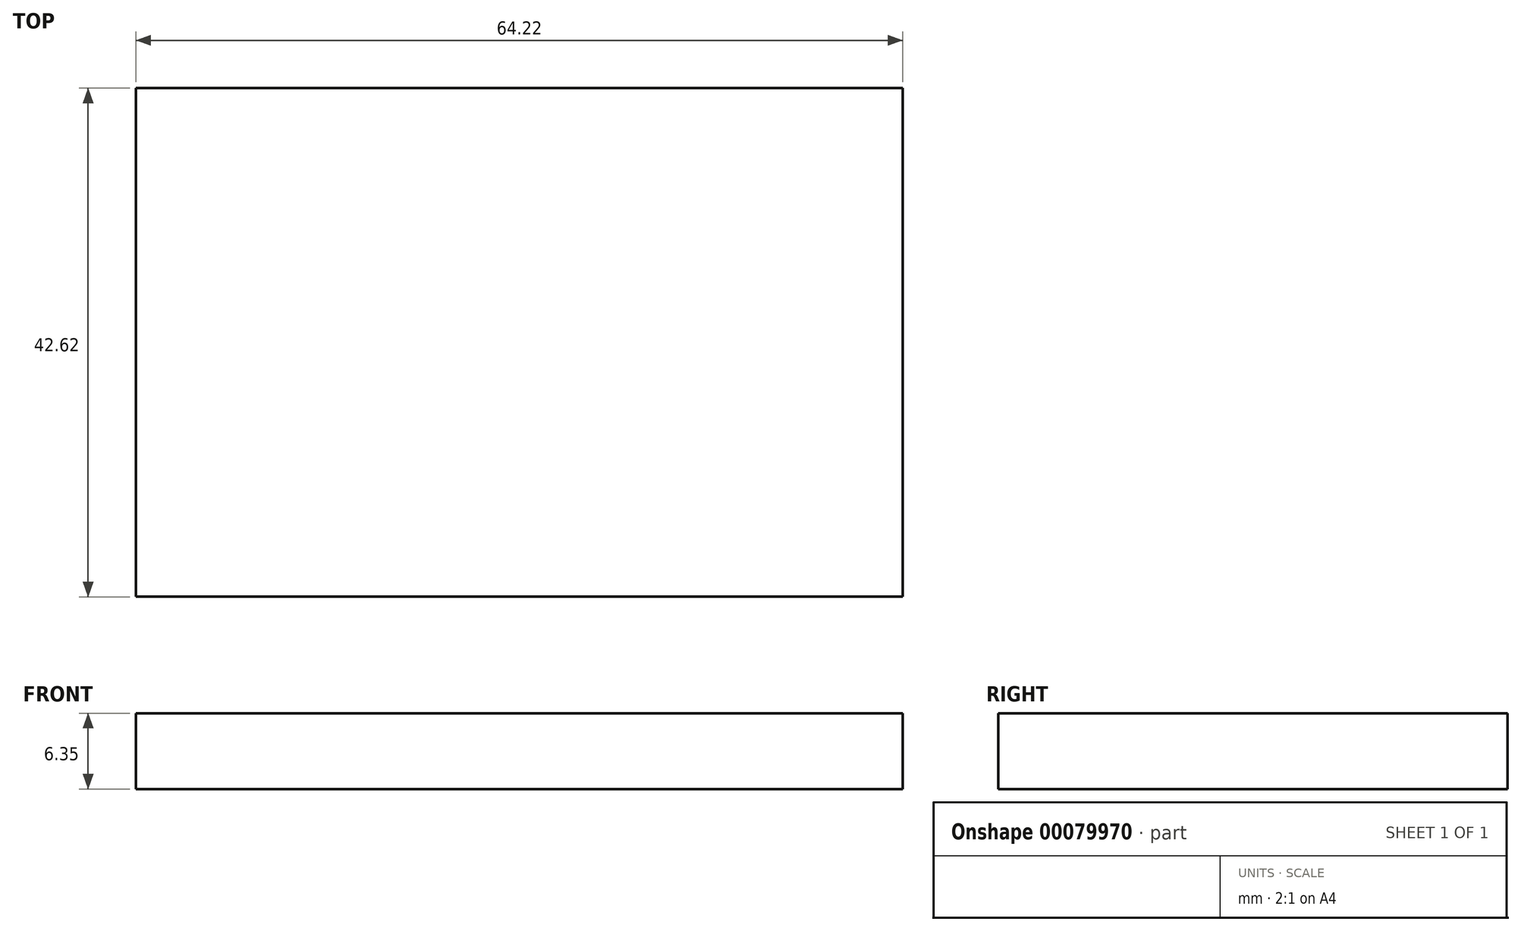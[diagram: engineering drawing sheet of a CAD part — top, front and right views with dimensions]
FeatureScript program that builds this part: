
annotation { "Feature Type Name" : "Feature", "Feature Type Description" : "" }
export const myFeature = defineFeature(function(context is Context, id is Id, definition is map)
    precondition{}
    {
        {
            var Q0;
            Q0=qCreatedBy(makeId("Top.planeOp"),FACE);
            var sketch = newSketch(context, id + "F0", { "sketchPlane" : qUnion([Q0])});
            skLineSegment(sketch, "E0.bottom", {"start": v(32.1, 21.3) * mm, "end": v(-32.1, 21.3) * mm});
            skLineSegment(sketch, "E0.top", {"start": v(32.1, -21.3) * mm, "end": v(-32.1, -21.3) * mm});
            skLineSegment(sketch, "E0.left", {"start": v(32.1, 21.3) * mm, "end": v(32.1, -21.3) * mm});
            skLineSegment(sketch, "E0.right", {"start": v(-32.1, 21.3) * mm, "end": v(-32.1, -21.3) * mm});
            skPoint(sketch, "E0.middle", {"position": v(0, 0) * mm});
            skSolve(sketch);
        }
        {
            var Q0;
            Q0 = qSketchRegion(id + "F0", true);
            extrude(context, id + "F1", {"entities" : qUnion([Q0]), "depth" : 6.35 * mm});
        }
        {
            var Q0;
            Q0=makeQuery(id+"F1.opExtrude","CAP_FACE",FACE,{"disambiguationData":[OSD([sQuery(id+"F0.wireOp",EDGE,"E0.bottom"),sQuery(id+"F0.wireOp",EDGE,"E0.top"),sQuery(id+"F0.wireOp",EDGE,"E0.left"),sQuery(id+"F0.wireOp",EDGE,"E0.right")])],"isStart":false});
            var sketch = newSketch(context, id + "F2", { "sketchPlane" : qUnion([Q0])});
            skArc(sketch, "E1", {"start": v(17.49, -6.97) * mm, "mid": v(11.87, -4.82) * mm, "end": v(9.73, -10.44) * mm});
            skLineSegment(sketch, "E2", {"start": v(17.49, -6.97) * mm, "end": v(13.6, -8.7) * mm});
            skSolve(sketch);
        }
        {
            var Q0;
            Q0=sQuery(id+"F2.wireOp",EDGE,"E1");
            var Q1;
            Q1=sQuery(id+"F2.wireOp",EDGE,"E2");
            revolve(context, id + "F3", {"bodyType" : ToolBodyType.SURFACE, "surfaceEntities" : qUnion([Q0]), "axis" : qUnion([Q1]), "revolveType" : RevolveType.FULL});
        }
    });
